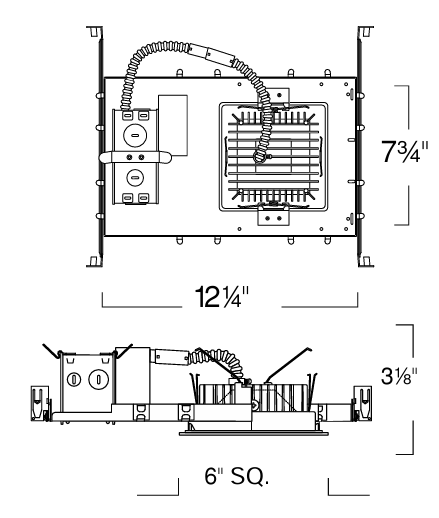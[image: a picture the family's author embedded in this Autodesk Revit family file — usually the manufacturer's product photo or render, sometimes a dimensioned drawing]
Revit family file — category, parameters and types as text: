
# Revit family: Alcon-14077-Revit-Family
name_source: partatom
category: Lighting Fixtures
units: mm (PartAtom-declared; Revit-internal decimal feet)

## family parameters
Always vertical = Yes
Cut with Voids When Loaded = Yes
Host = Ceiling
Light Source = Yes
Part Type = Normal
Room Calculation Point = No
Round Connector Dimension = Use Diameter
Shared = No

## types (1)
- Type 1
    Color Filter = 16777215
    Default Elevation = 0' - 0"
    Dimming Lamp Color Temperature Shift = <None>
    Driver = <By Category>
    Emit Shape Visible in Rendering = No
    Emit from Rectangle Length = 0' - 5"
    Emit from Rectangle Width = 0' - 5"
    Glass = Glass
    Housing = <By Category>
    Light Source = <By Category>
    Light Source Symbol Length = 10' - 0"
    Link To Product Page = https://www.alconlighting.com
    Manufacturer = Alcon Light
    Product Identity = Alcon Lighting 14077
    Reflector = <By Category>
    Spot Beam Angle = 30.00°
    Spot Field Angle = 90.00°
    Tilt Angle = 90.00°

## geometry (parser evidence)
native form markers: Sweep x1
no freeform markers — native parametric forms only
